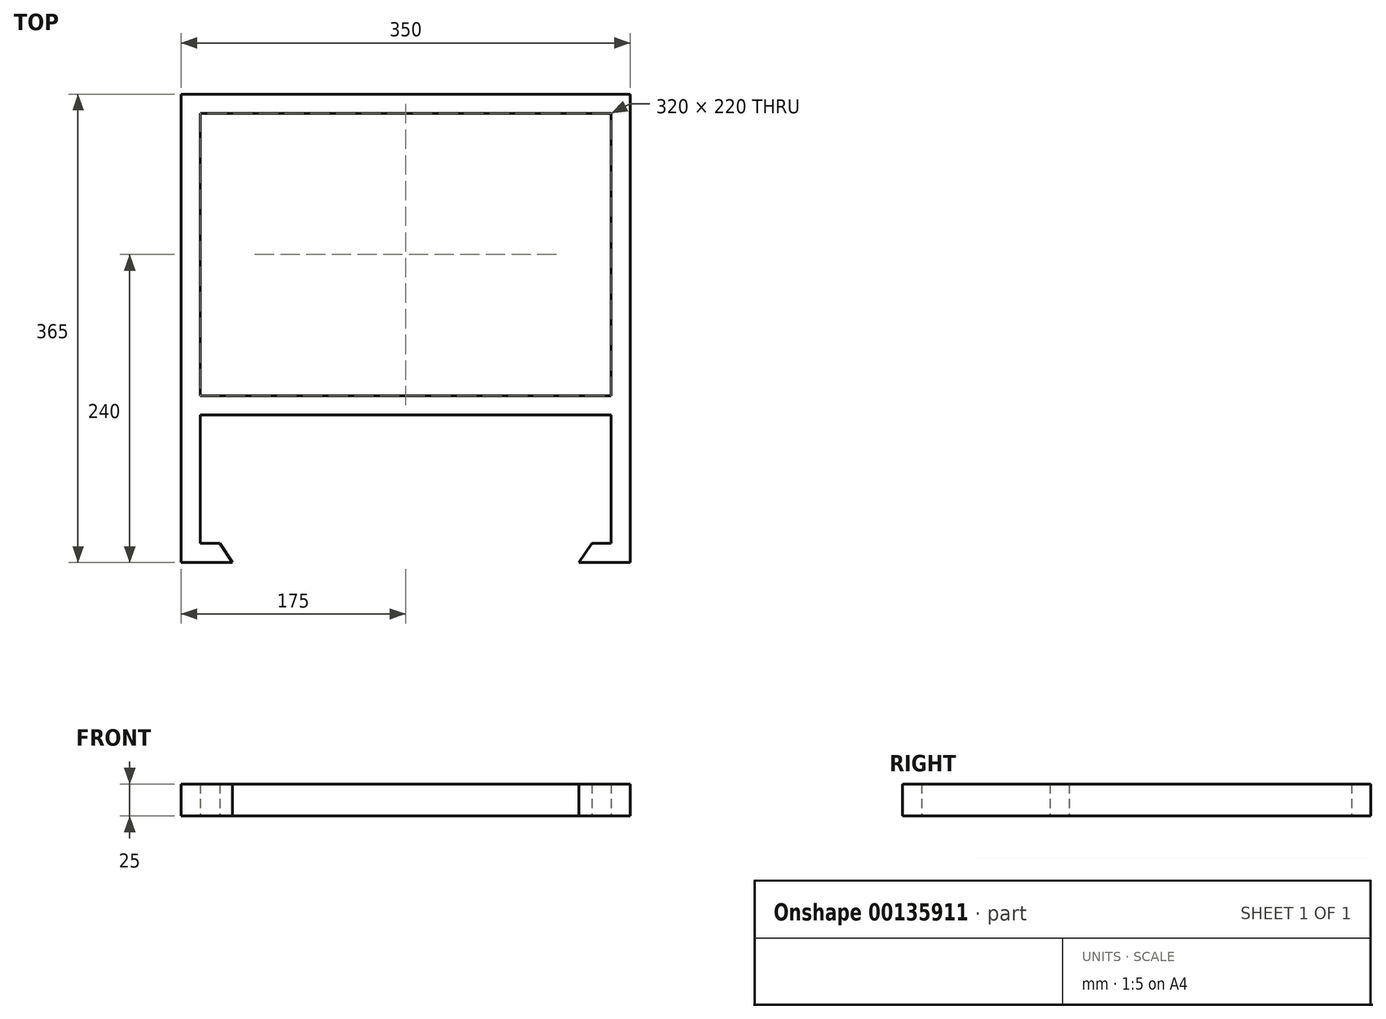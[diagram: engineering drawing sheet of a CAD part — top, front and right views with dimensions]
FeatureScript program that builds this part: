
annotation { "Feature Type Name" : "Feature", "Feature Type Description" : "" }
export const myFeature = defineFeature(function(context is Context, id is Id, definition is map)
    precondition{}
    {
        {
            var Q0;
            Q0=qCreatedBy(makeId("Top.planeOp"),FACE);
            var sketch = newSketch(context, id + "F0", { "sketchPlane" : qUnion([Q0])});
            skLineSegment(sketch, "E0.bottom", {"start": v(-160, 110) * mm, "end": v(160, 110) * mm, "construction": true});
            skLineSegment(sketch, "E0.top", {"start": v(-160, -110) * mm, "end": v(160, -110) * mm, "construction": true});
            skLineSegment(sketch, "E0.left", {"start": v(-160, 110) * mm, "end": v(-160, -110) * mm, "construction": true});
            skPoint(sketch, "E0.middle", {"position": v(0, 0) * mm});
            skLineSegment(sketch, "E1", {"start": v(-160, 110) * mm, "end": v(160, 110) * mm});
            skLineSegment(sketch, "E2", {"start": v(-160, 110) * mm, "end": v(-160, -110) * mm});
            skLineSegment(sketch, "E3", {"start": v(-160, -225) * mm, "end": v(-145, -225) * mm});
            skLineSegment(sketch, "E4.0", {"start": v(-175, 125) * mm, "end": v(-175, -240) * mm});
            skLineSegment(sketch, "E5.0", {"start": v(-175, 125) * mm, "end": v(175, 125) * mm});
            skLineSegment(sketch, "E6.0", {"start": v(-175, -240) * mm, "end": v(-135, -240) * mm});
            skLineSegment(sketch, "E7", {"start": v(-145, -225) * mm, "end": v(-135, -240) * mm});
            skLineSegment(sketch, "E8", {"start": v(0, -234.85) * mm, "end": v(0, 76.6) * mm, "construction": true});
            skLineSegment(sketch, "E9.MirrorCS", {"start": v(160, -225) * mm, "end": v(145, -225) * mm});
            skLineSegment(sketch, "E10.MirrorCS", {"start": v(145, -225) * mm, "end": v(135, -240) * mm});
            skLineSegment(sketch, "E11.MirrorCS", {"start": v(160, 110) * mm, "end": v(160, -110) * mm, "construction": true});
            skLineSegment(sketch, "E12.MirrorCS", {"start": v(175, -240) * mm, "end": v(135, -240) * mm});
            skLineSegment(sketch, "E13.MirrorCS", {"start": v(175, 125) * mm, "end": v(175, -240) * mm});
            skLineSegment(sketch, "E14", {"start": v(-160, -110) * mm, "end": v(160, -110) * mm});
            skLineSegment(sketch, "E15", {"start": v(-160, -125) * mm, "end": v(160, -125) * mm});
            skLineSegment(sketch, "E16.trimOffspring", {"start": v(-160, -125) * mm, "end": v(-160, -225) * mm});
            skLineSegment(sketch, "E17.MirrorCS", {"start": v(160, 110) * mm, "end": v(160, -110) * mm});
            skLineSegment(sketch, "E18.MirrorCS", {"start": v(160, -125) * mm, "end": v(160, -225) * mm});
            skSolve(sketch);
        }
        {
            var Q0;
            Q0=makeQuery(id+"F0.imprint","IMPRINT",FACE,{"disambiguationData":[TD([[makeQuery(id+"F0.imprint","IMPRINT",EDGE,{"derivedFrom":sQuery(id+"F0.wireOp",EDGE,"E1")}),1.0]])]});
            extrude(context, id + "F1", {"entities" : qUnion([Q0]), "depth" : 25 * mm});
        }
    });
